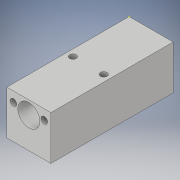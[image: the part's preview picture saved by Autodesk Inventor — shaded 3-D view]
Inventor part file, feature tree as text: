
AUTODESK INVENTOR PART (.ipt)
format: ipt  version: 2019 (Build 230136000, 136)  size: 122,368 bytes
history: native  units: mm
features: sketch x5, extrude x4
ambient origin geometry x8: Origin, YZ Plane, XZ Plane, XY Plane, X Axis, Y Axis, Z Axis, Center Point
bodies: Solid1 (feature_tree)
feature tree (9):
  extrude  "Extrusion1"  Depth=20.0mm
  extrude  "Extrusion2"  Depth=55.5mm
  extrude  "Extrusion3"  Depth=28.5mm
  extrude  "Extrusion4"  Depth=3.0mm
  sketch  "Sketch5"  dims[d9=40.0mm d10=0.0mm d11=3.0mm d12=3.0mm d13=14.0mm d14=3.0mm d15=3.0mm d16=10.0mm d17=0.0mm d18=6.0mm d19=10.0mm d20=10.0mm d21=0.0mm d22=4.5mm]
  sketch  "Sketch1"  dims[d0=20.0mm d1=20.0mm]
  sketch  "Sketch2"  dims[d2=55.5mm d3=0.0mm d4=14.0mm]
  sketch  "Sketch3"  dims[d5=3.0mm d6=28.5mm]
  sketch  "Sketch4"  dims[d7=3.0mm d8=3.0mm]
